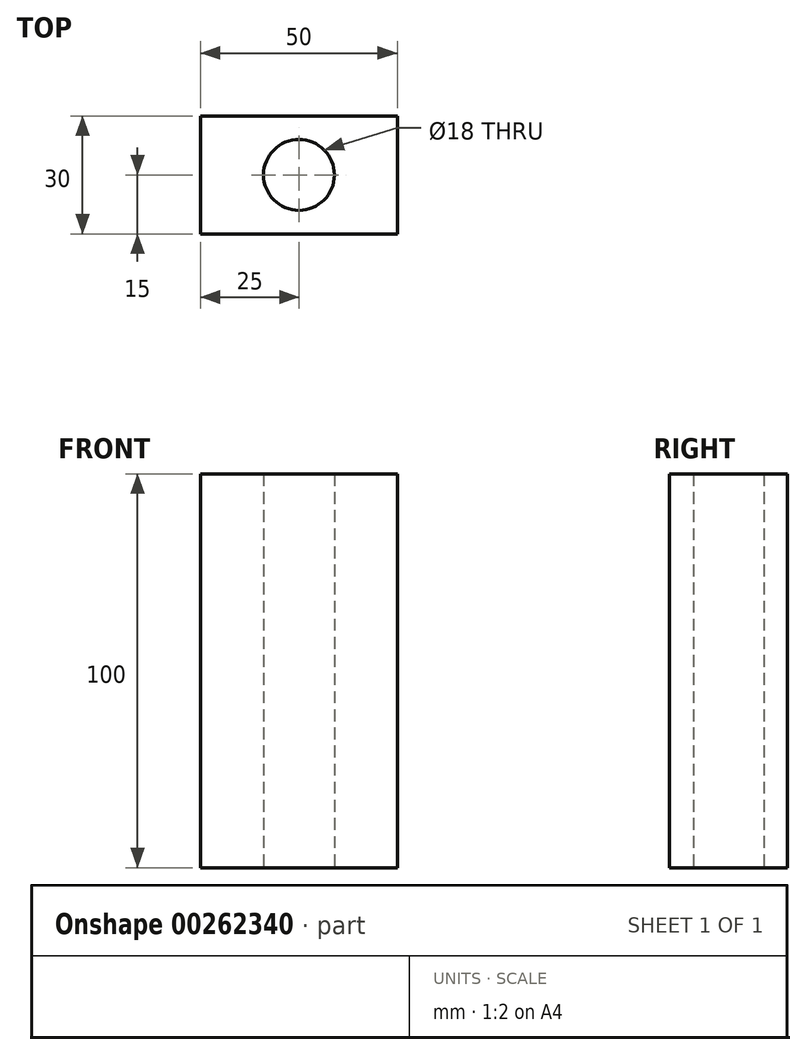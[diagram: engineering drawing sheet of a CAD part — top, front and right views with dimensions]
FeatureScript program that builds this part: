
annotation { "Feature Type Name" : "Feature", "Feature Type Description" : "" }
export const myFeature = defineFeature(function(context is Context, id is Id, definition is map)
    precondition{}
    {
        {
            var Q0;
            Q0=qCreatedBy(makeId("Top.planeOp"),FACE);
            var sketch = newSketch(context, id + "F0", { "sketchPlane" : qUnion([Q0])});
            skLineSegment(sketch, "E0.bottom", {"start": v(-25, -15) * mm, "end": v(25, -15) * mm});
            skLineSegment(sketch, "E0.top", {"start": v(-25, 15) * mm, "end": v(25, 15) * mm});
            skLineSegment(sketch, "E0.left", {"start": v(-25, -15) * mm, "end": v(-25, 15) * mm});
            skLineSegment(sketch, "E0.right", {"start": v(25, -15) * mm, "end": v(25, 15) * mm});
            skPoint(sketch, "E0.middle", {"position": v(0, 0) * mm});
            skCircle(sketch, "E1", {"center": v(0, 0) * mm, "radius": 9 * mm});
            skPoint(sketch, "E2.endSnap0", {"position": v(0, -15) * mm});
            skLineSegment(sketch, "E3", {"start": v(-7.34, -15) * mm, "end": v(-7.34, -15) * mm});
            skSolve(sketch);
        }
        {
            var Q0;
            Q0 = qSketchRegion(id + "F0", true);
            extrude(context, id + "F1", {"entities" : qUnion([Q0]), "depth" : 100 * mm});
        }
    });
